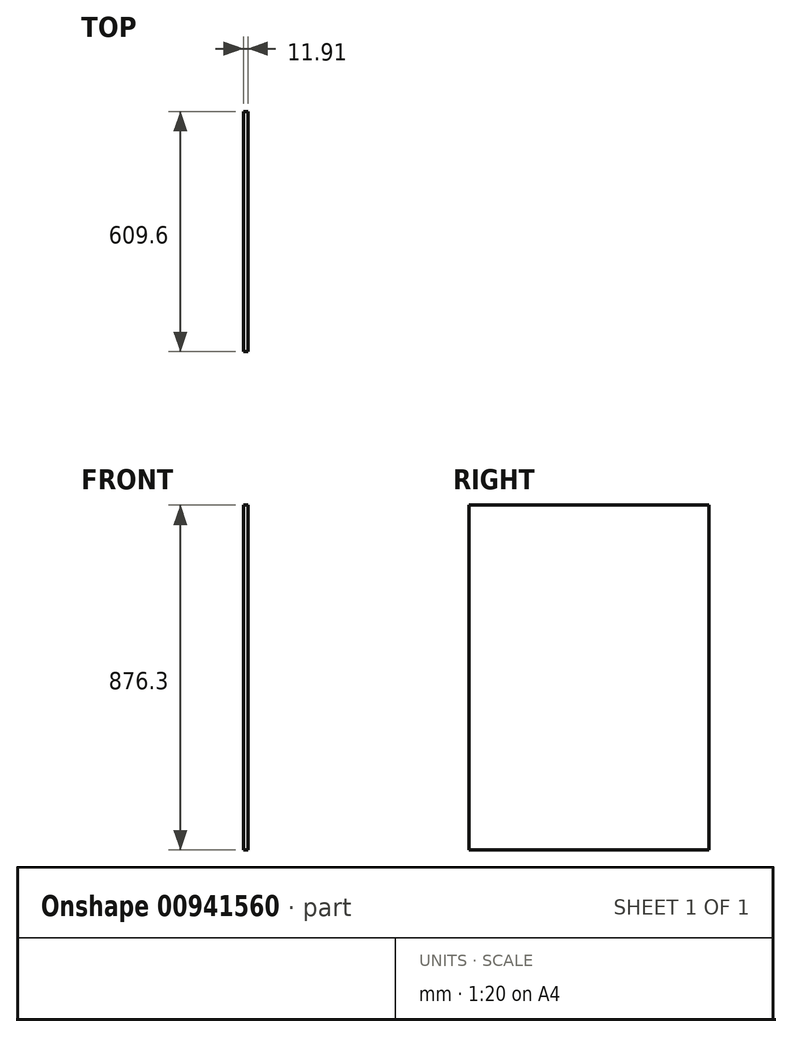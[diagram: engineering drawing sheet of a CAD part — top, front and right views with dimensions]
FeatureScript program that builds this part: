
annotation { "Feature Type Name" : "Feature", "Feature Type Description" : "" }
export const myFeature = defineFeature(function(context is Context, id is Id, definition is map)
    precondition{}
    {
        {
            var Q0;
            Q0=qCreatedBy(makeId("Right.planeOp"),FACE);
            var sketch = newSketch(context, id + "F0", { "sketchPlane" : qUnion([Q0])});
            skLineSegment(sketch, "E0.bottom", {"start": v(304.8, 438.15) * mm, "end": v(-304.8, 438.15) * mm});
            skLineSegment(sketch, "E0.top", {"start": v(304.8, -438.15) * mm, "end": v(-304.8, -438.15) * mm});
            skLineSegment(sketch, "E0.left", {"start": v(304.8, 438.15) * mm, "end": v(304.8, -438.15) * mm});
            skLineSegment(sketch, "E0.right", {"start": v(-304.8, 438.15) * mm, "end": v(-304.8, -438.15) * mm});
            skPoint(sketch, "E0.middle", {"position": v(0, 0) * mm});
            skSolve(sketch);
        }
        {
            var Q0;
            Q0 = qSketchRegion(id + "F0", true);
            extrude(context, id + "F1", {"entities" : qUnion([Q0]), "depth" : 11.9 * mm, "offsetDistance" : 25.4 * mm});
        }
    });
